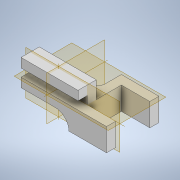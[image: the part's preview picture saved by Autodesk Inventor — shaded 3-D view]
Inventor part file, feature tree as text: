
AUTODESK INVENTOR PART (.ipt)
format: ipt  version: 2022.4 (Build 264492010, 492A)  size: 176,640 bytes
history: native  units: mm
features: extrude x4, sketch x4, mirror x1
ambient origin geometry x8: Origin, YZ Plane, XZ Plane, XY Plane, X Axis, Y Axis, Z Axis, Center Point
bodies: Solid1 (feature_tree)
feature tree (9):
  extrude  "Extrusion1"  Depth=3.0mm
  extrude  "Extrusion2"  Depth=1.6mm
  sketch  "Sketch4"  dims[d3=3.2mm d4=1.6mm]
  sketch  "Sketch5"  dims[d6=4.0mm d7=1.6mm]
  extrude  "Extrusion3"  Depth=1.6mm
  extrude  "Extrusion4"  Depth=10.0mm TaperAngle=0.0deg
  mirror  "Mirror1"
  sketch  "Sketch3"  dims[d1=6.0mm d2=3.0mm]
  sketch  "Sketch6"  dims[d8=1.4mm d10=10.0mm d11=0.0mm d12=1.6mm d14=1.6mm d15=1.6mm d17=2.4mm d18=0.0mm d19=0.0mm d20=1.6mm d21=1.6mm d22=5.0mm d23=0.0mm d24=1.6mm d25=1.6mm d26=1.6mm d27=0.0mm d28=0.0mm]
